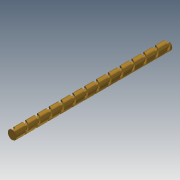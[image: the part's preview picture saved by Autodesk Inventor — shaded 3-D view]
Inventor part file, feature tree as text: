
AUTODESK INVENTOR PART (.ipt)
format: ipt  version: 2014 SP1 (Build 180222100, 222)  size: 195,072 bytes
history: native  units: in
note: dims shown in document units (in); Inventor stores cm internally (conversion verified against a paired STEP export)
features: sketch x2, extrude x1, helix x1
ambient origin geometry x8: Origin, YZ Plane, XZ Plane, XY Plane, X Axis, Y Axis, Z Axis, Center Point
bodies: Solid1 (feature_tree)
feature tree (4):
  extrude  "Extrusion1"  Depth=2.0748in TaperAngle=0.0deg
  helix  "Coil1"  [1 undecoded]
  sketch  "Sketch1"  dims[d0=0.1181in d1=2.0748in d2=0.0in d7=0.0354in]
  sketch  "Sketch3"  dims[d8=0.0394in d9=0.0394in d10=0.1575in d11=0.3937in d12=11.811in d13=0.0in d14=90.0deg d15=90.0deg d16=0.0in d17=0.0in]
note: 1 required parameter value undecoded (feature->parameter linkage not recoverable at this tier; creation-order binding heuristic only, values carry confidence <= 0.55)
